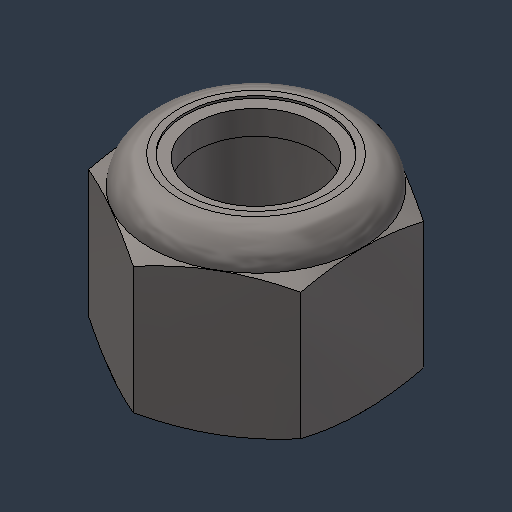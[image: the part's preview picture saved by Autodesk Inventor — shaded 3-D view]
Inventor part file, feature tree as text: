
AUTODESK INVENTOR PART (.ipt)
format: ipt  version: 2024.3 (Build 283343000, 343)  size: 178,176 bytes
history: native  units: mm (DEFAULTED — no unit token found)
features: other x1, revolve x1
ambient origin geometry x8: Origin, YZ Plane, XZ Plane, XY Plane, X Axis, Y Axis, Z Axis, Center Point
bodies: Solid1 (feature_tree), Solid2 (feature_tree)
feature tree (2):
  other  "Cut-Revolve2"
  revolve  "Revolve1"  [1 undecoded]
note: 1 required parameter value undecoded (feature->parameter linkage not recoverable at this tier; creation-order binding heuristic only, values carry confidence <= 0.55)
